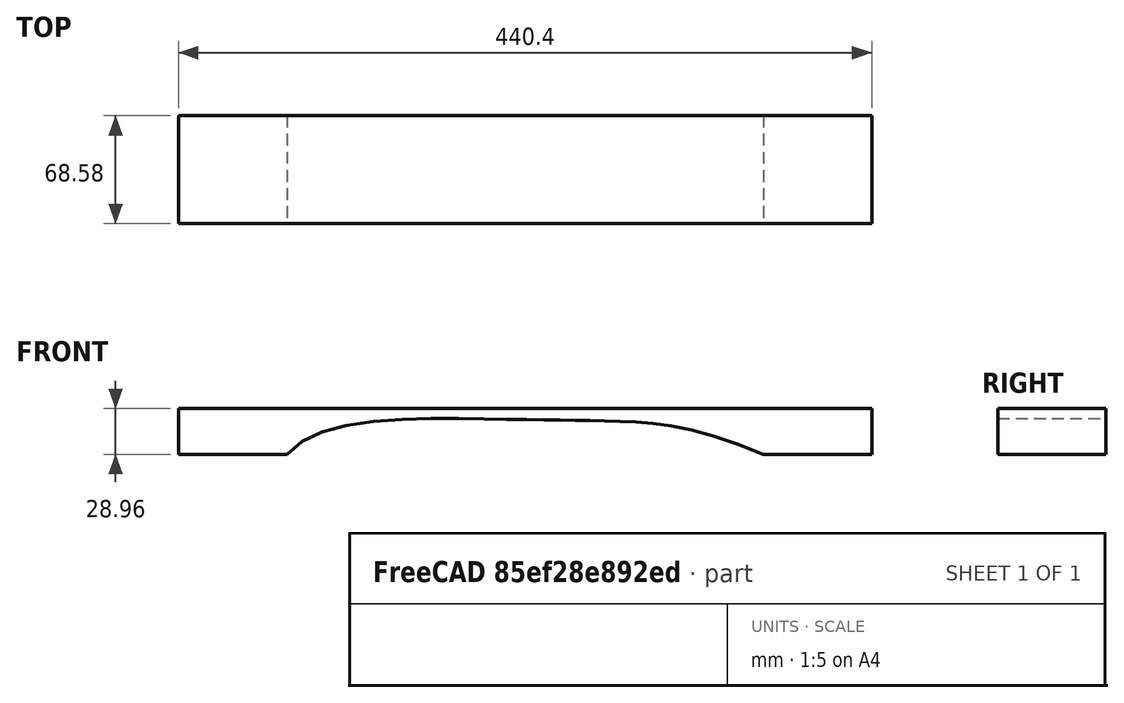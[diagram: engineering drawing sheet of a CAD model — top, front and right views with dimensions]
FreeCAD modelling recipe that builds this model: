
FCSTD DOCUMENT  (FreeCAD 0.20R29410 (Git))
Label: Single_Bar16
License: All rights reserved
LicenseURL: http://en.wikipedia.org/wiki/All_rights_reserved
objects: Sketcher::SketchObject×1, Part::Extrusion×1, Fem::FemSolverObjectPython×1, App::MaterialObjectPython×1, Fem::ConstraintDisplacement×1, Fem::FemMeshShapeNetgenObject×1, Fem::FemAnalysis×1
note: 2 computed .brp shape members not serialized (recipe doc carries the construction recipe); baked Part::Feature solids carry a one-line shape summary decoded from their .brp

FEATURE [Sketcher::SketchObject] Sketch
  FullyConstrained = true
  Placement = pos=(0,0,0) rot=(1,0,0;1.5708rad)
  sketch-geometry (12):
    g0: LineSegment StartX=68.98 StartY=0 StartZ=0 EndX=0 EndY=0 EndZ=0
    g1: LineSegment StartX=0 StartY=0 StartZ=0 EndX=0 EndY=28.96 EndZ=0
    g2: LineSegment StartX=0 StartY=28.96 StartZ=0 EndX=440.4 EndY=28.96 EndZ=0
    g3: LineSegment StartX=440.4 StartY=28.96 StartZ=0 EndX=440.4 EndY=0 EndZ=0
    g4: LineSegment StartX=440.4 StartY=0 StartZ=0 EndX=371.42 EndY=0 EndZ=0
    g5-g10: Circle x6 (B-spline internal-alignment scaffolding for g11; pole/knot coordinates omitted)
    g11: BSplineCurve PolesCount=6 KnotsCount=4 Degree=3 IsPeriodic=0
  constraints (38):
    c: DistanceX(g0) = 0
    c: DistanceY(g0) = 0
    c: Distance(g1,g1) = 28.96
    c: Distance(g2,g2) = 440.4
    c: DistanceX(g0,g0) = 68.98
    c: DistanceX(g4,g4) = 68.98
    c: Horizontal(g0)
    c: Vertical(g1)
    c: Horizontal(g2)
    c: Vertical(g3)
    c: Horizontal(g4)
    c: Equal(g3,g1)
    c: Coincident(g0,g1)
    c: Coincident(g1,g2)
    c: Coincident(g2,g3)
    c: Coincident(g3,g4)
    c: DistanceX(g6) = 326.75
    c: DistanceY(g6) = 19.25
    c: DistanceX(g7) = 269.78
    c: DistanceY(g7) = 21.62
    c: DistanceX(g8) = 209.11
    c: DistanceY(g8) = 21.95
    c: DistanceX(g9) = 88.11
    c: DistanceY(g9) = 24.09
    c: Weight(g5) = 1
    c: InternalAlignment(g5,g11)
    c: Weight(g6) = 1
    c: InternalAlignment(g6,g11)
    c: Weight(g7) = 1
    c: InternalAlignment(g7,g11)
    c: Weight(g8) = 1
    c: InternalAlignment(g8,g11)
    c: Weight(g9) = 1
    c: InternalAlignment(g9,g11)
    c: Weight(g10) = 1
    c: InternalAlignment(g10,g11)
    c: Coincident(g4,g11)
    c: Coincident(g0,g11)
FEATURE [Part::Extrusion] Bar
  Base = -> Sketch
  Dir = (0,-1,-3e-16)
  DirMode = 2
  FaceMakerClass = Part::FaceMakerBullseye
  LengthFwd = 68.58
  LengthRev = 0
  Solid = true
  Symmetric = false
FEATURE [Fem::FemSolverObjectPython] SolverCcxTools  # FEM object (typed FeaturePython)
  AnalysisType = 0
  BeamShellResultOutput3D = false
  BucklingFactors = 1
  EigenmodeHighLimit = 20000
  EigenmodeLowLimit = 20
  EigenmodesCount = 12
  GeometricalNonlinearity = 0
  IterationsControlParameterCutb = 0.25,0.5,0.75,0.85,,,1.5,
  IterationsControlParameterIter = 4,8,9,200,10,400,,200,,
  IterationsControlParameterTimeUse = false
  IterationsThermoMechMaximum = 2000
  IterationsUserDefinedIncrementations = false
  IterationsUserDefinedTimeStepLength = false
  MaterialNonlinearity = 0
  MatrixSolverType = 0
  SplitInputWriter = false
  ThermoMechSteadyState = false
  TimeEnd = 1
  TimeInitialStep = 0.01
FEATURE [App::MaterialObjectPython] MaterialSolid  # material (typed FeaturePython)
  Category = 0
  Material = CompressiveStrength=4300 kPa; Density=430 kg/m^3; Name=Wood-Chestnut; PoissonRatio=0.32; ShearModulus=7.4 MPa; UltimateTensileStrength=59.0 MPa; YoungsModulus=8500 MPa
FEATURE [Fem::ConstraintDisplacement] FemConstraintDisplacement
  NormalDirection = (0,3e-16,-1)
  Normals = (116) [(0,3.33067e-16,-1),(0,3.33067e-16,-1),(0,3.33067e-16,-1),(0,3.33067e-16,-1),(0,3.33067e-16,-1),(0,3.33067e-16,-1),(0,3.33067e-16,-1),+109 more]
  Points = (116) [(68.98,-68.58,-2.28417e-14),(45.9867,-68.58,-2.28417e-14),(22.9933,-68.58,-2.28417e-14),(0,-68.58,-2.28417e-14),(68.98,-45.72,-1.52278e-14),+111 more]
  References = -> [Bar]
  rotxFix = false
  rotxFree = true
  rotyFix = false
  rotyFree = true
  rotzFix = false
  rotzFree = true
  xDisplacement = 0
  xFix = false
  xFree = true
  xRotation = 0
  yDisplacement = 0
  yFix = true
  yFree = false
  yRotation = 0
  zDisplacement = 0
  zFix = false
  zFree = true
  zRotation = 0
FEATURE [Fem::FemMeshShapeNetgenObject] FEMMeshNetgen
  Fineness = 4
  GrowthRate = 0.3
  MaxSize = 10
  NbSegsPerEdge = 1
  NbSegsPerRadius = 2
  Optimize = true
  SecondOrder = true
  Shape = -> Bar
FEATURE [Fem::FemAnalysis] Analysis
  Group = -> [SolverCcxTools,MaterialSolid,FemConstraintDisplacement,FEMMeshNetgen]
